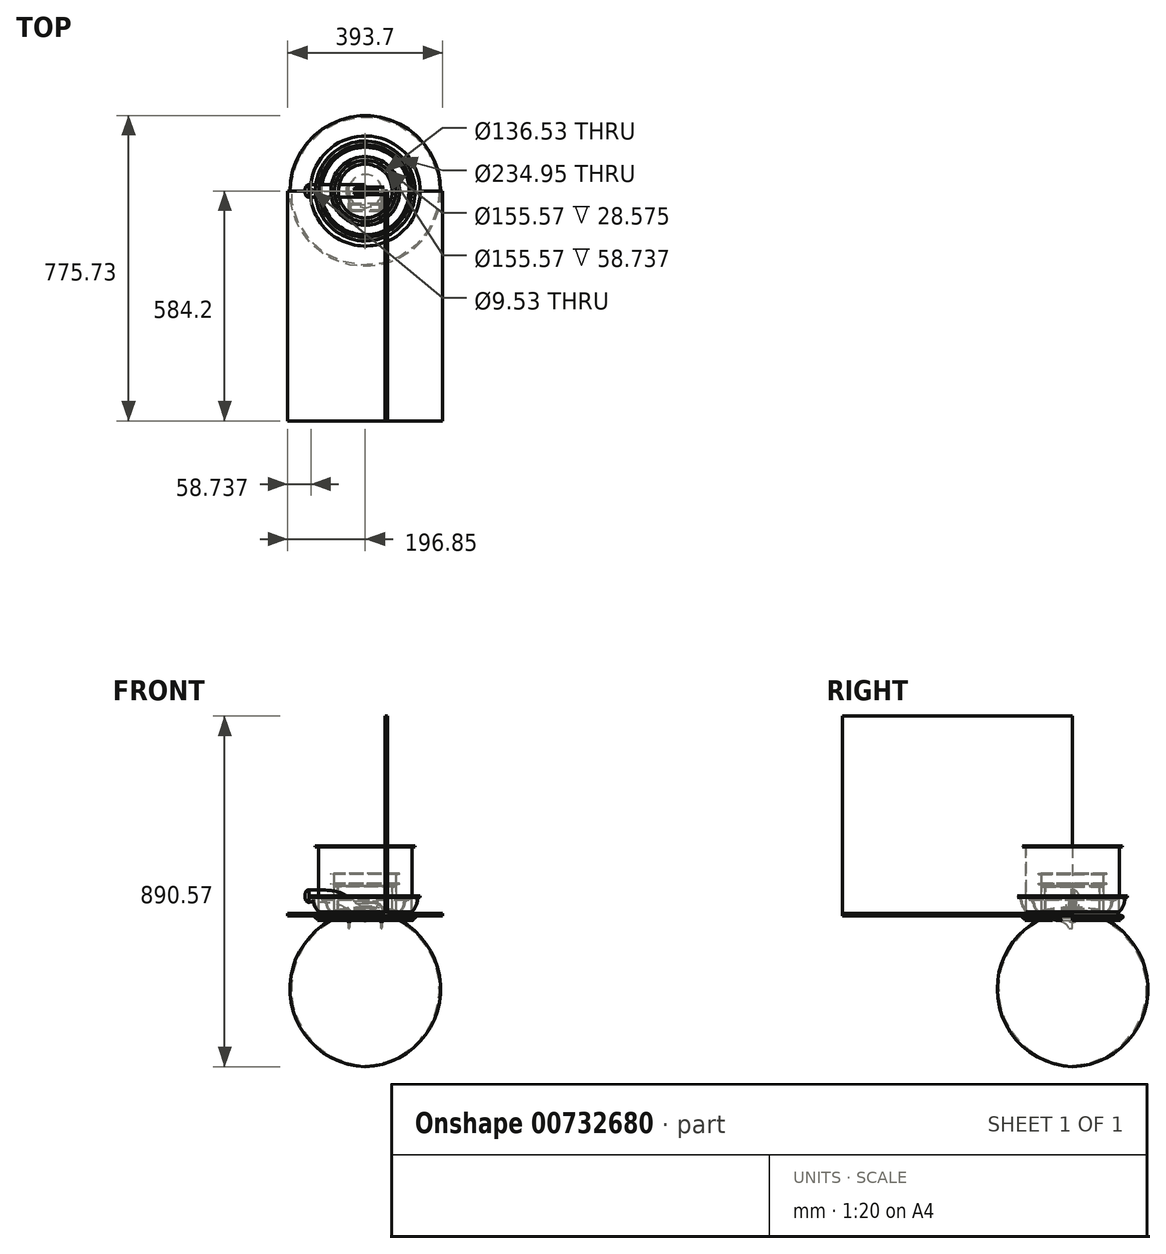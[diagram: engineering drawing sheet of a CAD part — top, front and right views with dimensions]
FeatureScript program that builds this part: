
annotation { "Feature Type Name" : "Feature", "Feature Type Description" : "" }
export const myFeature = defineFeature(function(context is Context, id is Id, definition is map)
    precondition{}
    {
        {
            var Q0;
            Q0=qCreatedBy(makeId("Front.planeOp"),FACE);
            var sketch = newSketch(context, id + "F0", { "sketchPlane" : qUnion([Q0])});
            skLineSegment(sketch, "E0", {"start": v(0, 0) * mm, "end": v(-61.91, 0) * mm});
            skLineSegment(sketch, "E1", {"start": v(-61.91, 0) * mm, "end": v(-69.85, 10.16) * mm});
            skLineSegment(sketch, "E2", {"start": v(-69.85, 10.16) * mm, "end": v(-69.85, 71.44) * mm});
            skLineSegment(sketch, "E3", {"start": v(-73.03, 74.61) * mm, "end": v(-77.79, 74.61) * mm});
            skLineSegment(sketch, "E4", {"start": v(-77.79, 74.61) * mm, "end": v(-77.79, 76.2) * mm});
            skLineSegment(sketch, "E5", {"start": v(-77.79, 76.2) * mm, "end": v(-71.44, 76.2) * mm});
            skLineSegment(sketch, "E6", {"start": v(-68.26, 73.02) * mm, "end": v(-68.26, 15.87) * mm});
            skLineSegment(sketch, "E7", {"start": v(-61.91, 9.52) * mm, "end": v(0, 9.53) * mm});
            skLineSegment(sketch, "E8", {"start": v(0, 9.53) * mm, "end": v(0, 0) * mm});
            skArc(sketch, "E9.filletArc", {"start": v(-68.26, 15.87) * mm, "mid": v(-66.4, 11.38) * mm, "end": v(-61.91, 9.52) * mm});
            skPoint(sketch, "E10.visualSharp", {"position": v(-69.85, 74.61) * mm});
            skArc(sketch, "E10.filletArc", {"start": v(-69.85, 71.44) * mm, "mid": v(-70.78, 73.68) * mm, "end": v(-73.03, 74.61) * mm});
            skPoint(sketch, "E11.visualSharp", {"position": v(-68.26, 76.2) * mm});
            skArc(sketch, "E11.filletArc", {"start": v(-68.26, 73.02) * mm, "mid": v(-69.2, 75.27) * mm, "end": v(-71.44, 76.2) * mm});
            skSolve(sketch);
        }
        {
            var Q0;
            Q0=makeQuery(id+"F0.imprint","IMPRINT",FACE,{"disambiguationData":[TD([[makeQuery(id+"F0.imprint","IMPRINT",EDGE,{"derivedFrom":sQuery(id+"F0.wireOp",EDGE,"E0")}),-1.0]])]});
            var Q1;
            Q1=sQuery(id+"F0.wireOp",EDGE,"E8");
            revolve(context, id + "F1", {"surfaceOperationType" : NewSurfaceOperationType.NEW, "entities" : qUnion([Q0]), "axis" : qUnion([Q1]), "revolveType" : RevolveType.FULL});
        }
        {
            var Q0;
            Q0=qCreatedBy(makeId("Front.planeOp"),FACE);
            var sketch = newSketch(context, id + "F2", { "sketchPlane" : qUnion([Q0])});
            skLineSegment(sketch, "E12", {"start": v(0, 0) * mm, "end": v(-71.44, 0) * mm});
            skLineSegment(sketch, "E13", {"start": v(-71.44, 0) * mm, "end": v(-79.38, 10.16) * mm});
            skLineSegment(sketch, "E14", {"start": v(-79.38, 10.16) * mm, "end": v(-79.38, 77.79) * mm});
            skLineSegment(sketch, "E15", {"start": v(-82.55, 80.96) * mm, "end": v(-87.31, 80.96) * mm});
            skLineSegment(sketch, "E16", {"start": v(-87.31, 80.96) * mm, "end": v(-87.31, 82.55) * mm});
            skLineSegment(sketch, "E17", {"start": v(-87.31, 82.55) * mm, "end": v(-80.96, 82.55) * mm});
            skLineSegment(sketch, "E18", {"start": v(-77.79, 79.38) * mm, "end": v(-77.79, 15.88) * mm});
            skLineSegment(sketch, "E19", {"start": v(-71.44, 9.52) * mm, "end": v(0, 9.53) * mm});
            skLineSegment(sketch, "E20", {"start": v(0, 9.53) * mm, "end": v(0, 0) * mm});
            skArc(sketch, "E21.filletArc", {"start": v(-77.79, 15.88) * mm, "mid": v(-75.93, 11.38) * mm, "end": v(-71.44, 9.53) * mm});
            skPoint(sketch, "E22.visualSharp", {"position": v(-79.38, 80.96) * mm});
            skArc(sketch, "E22.filletArc", {"start": v(-79.38, 77.79) * mm, "mid": v(-80.3, 80.03) * mm, "end": v(-82.55, 80.96) * mm});
            skPoint(sketch, "E23.visualSharp", {"position": v(-77.79, 82.55) * mm});
            skArc(sketch, "E23.filletArc", {"start": v(-77.79, 79.38) * mm, "mid": v(-78.72, 81.62) * mm, "end": v(-80.96, 82.55) * mm});
            skSolve(sketch);
        }
        {
            var Q0;
            Q0 = qSketchRegion(id + "F2", true);
            var Q1;
            Q1=sQuery(id+"F2.wireOp",EDGE,"E20");
            revolve(context, id + "F3", {"surfaceOperationType" : NewSurfaceOperationType.NEW, "entities" : qUnion([Q0]), "axis" : qUnion([Q1]), "revolveType" : RevolveType.FULL});
        }
        {
            var Q0;
            Q0=qCreatedBy(makeId("Front.planeOp"),FACE);
            var sketch = newSketch(context, id + "F4", { "sketchPlane" : qUnion([Q0])});
            skLineSegment(sketch, "E24", {"start": v(0, 0) * mm, "end": v(-71.44, 0) * mm});
            skLineSegment(sketch, "E25", {"start": v(-71.44, 0) * mm, "end": v(-79.38, 10.16) * mm});
            skLineSegment(sketch, "E26", {"start": v(-79.38, 10.16) * mm, "end": v(-79.38, 103.19) * mm});
            skLineSegment(sketch, "E27", {"start": v(-82.55, 106.36) * mm, "end": v(-87.31, 106.36) * mm});
            skLineSegment(sketch, "E28", {"start": v(-87.31, 106.36) * mm, "end": v(-87.31, 107.95) * mm});
            skLineSegment(sketch, "E29", {"start": v(-87.31, 107.95) * mm, "end": v(-80.96, 107.95) * mm});
            skLineSegment(sketch, "E30", {"start": v(-77.79, 104.78) * mm, "end": v(-77.79, 15.87) * mm});
            skLineSegment(sketch, "E31", {"start": v(-71.44, 9.52) * mm, "end": v(0, 9.53) * mm});
            skLineSegment(sketch, "E32", {"start": v(0, 9.53) * mm, "end": v(0, 0) * mm});
            skArc(sketch, "E33.filletArc", {"start": v(-77.79, 15.87) * mm, "mid": v(-75.93, 11.38) * mm, "end": v(-71.44, 9.52) * mm});
            skPoint(sketch, "E34.visualSharp", {"position": v(-79.38, 106.36) * mm});
            skArc(sketch, "E34.filletArc", {"start": v(-79.38, 103.19) * mm, "mid": v(-80.3, 105.43) * mm, "end": v(-82.55, 106.36) * mm});
            skPoint(sketch, "E35.visualSharp", {"position": v(-77.79, 107.95) * mm});
            skArc(sketch, "E35.filletArc", {"start": v(-77.79, 104.78) * mm, "mid": v(-78.72, 107.02) * mm, "end": v(-80.96, 107.95) * mm});
            skSolve(sketch);
        }
        {
            var Q0;
            Q0 = qSketchRegion(id + "F4", true);
            var Q1;
            Q1=sQuery(id+"F4.wireOp",EDGE,"E32");
            revolve(context, id + "F5", {"surfaceOperationType" : NewSurfaceOperationType.NEW, "entities" : qUnion([Q0]), "axis" : qUnion([Q1]), "revolveType" : RevolveType.FULL});
        }
        {
            var Q0;
            Q0=qCreatedBy(makeId("Front.planeOp"),FACE);
            var sketch = newSketch(context, id + "F6", { "sketchPlane" : qUnion([Q0])});
            skFitSpline(sketch, "E36", {"points": [v(0, 0) * mm, v(-53.98, 39.09) * mm, v(-152.4, 50.8) * mm], "startDerivative": vector(-187.57, 165.8) * mm, "endDerivative": vector(-373.43, -7.39) * mm});
            skSolve(sketch);
        }
        {
            var Q0;
            Q0=qCreatedBy(makeId("Right.planeOp"),FACE);
            var sketch = newSketch(context, id + "F7", { "sketchPlane" : qUnion([Q0])});
            skCircle(sketch, "E37", {"center": v(0, 0) * mm, "radius": 15.88 * mm});
            skSolve(sketch);
        }
        {
            var Q0;
            Q0 = qSketchRegion(id + "F7", true);
            var Q1;
            Q1=sQuery(id+"F6.wireOp",EDGE,"E36");
            sweep(context, id + "F8", {"profiles" : qUnion([Q0]), "path" : qUnion([Q1]), "keepProfileOrientation" : true});
        }
        {
            var Q0;
            Q0=makeQuery(id+"F8.opSweep","CAP_EDGE",EDGE,{"disambiguationData":[OSD([sQuery(id+"F6.wireOp",VERTEX,"E36.end"),sQuery(id+"F7.wireOp",EDGE,"E37")])],"isStart":false});
            fillet(context, id + "F9", {"entities" : qUnion([Q0]), "radius" : 9.52 * mm, "tangentPropagation" : true, "allowEdgeOverflow" : false});
        }
        {
            var Q0;
            Q0=qCreatedBy(makeId("Top.planeOp"),FACE);
            var sketch = newSketch(context, id + "F10", { "sketchPlane" : qUnion([Q0])});
            skCircle(sketch, "E38", {"center": v(-138.11, 0) * mm, "radius": 4.76 * mm});
            skSolve(sketch);
        }
        {
            var Q0;
            Q0=makeQuery(id+"F10.imprint","IMPRINT",FACE,{"disambiguationData":[TD([[makeQuery(id+"F10.imprint","IMPRINT",EDGE,{"derivedFrom":sQuery(id+"F10.wireOp",EDGE,"E38")}),1.0]])]});
            extrude(context, id + "F11", {"entities" : qUnion([Q0]), "operationType" : NewBodyOperationType.REMOVE, "depth" : 76.2 * mm, "offsetDistance" : 25.4 * mm});
        }
        {
            var Q0;
            Q0=qCreatedBy(makeId("Front.planeOp"),FACE);
            var sketch = newSketch(context, id + "F12", { "sketchPlane" : qUnion([Q0])});
            skArc(sketch, "E39", {"start": v(0, 12.7) * mm, "mid": v(-38.34, 10.18) * mm, "end": v(-75.46, 0.28) * mm});
            skLineSegment(sketch, "E40", {"start": v(0, 0) * mm, "end": v(0, 12.7) * mm, "construction": true});
            skPoint(sketch, "E41.orphan", {"position": v(63.8, 0) * mm});
            skArc(sketch, "E42.0", {"start": v(0, 9.53) * mm, "mid": v(-35.13, 7.47) * mm, "end": v(-69.31, -0.9) * mm});
            skArc(sketch, "E43", {"start": v(-75.46, 0.28) * mm, "mid": v(-76.34, 0.78) * mm, "end": v(-77, 0) * mm});
            skLineSegment(sketch, "E44", {"start": v(-77, 0) * mm, "end": v(-77, -3.97) * mm});
            skLineSegment(sketch, "E45", {"start": v(-76.2, -4.76) * mm, "end": v(-71.44, -4.76) * mm});
            skLineSegment(sketch, "E46", {"start": v(-70.64, -5.56) * mm, "end": v(-70.64, -11.11) * mm});
            skLineSegment(sketch, "E47", {"start": v(-70.64, -11.11) * mm, "end": v(-69.85, -11.11) * mm});
            skLineSegment(sketch, "E48", {"start": v(-69.85, -11.11) * mm, "end": v(-69.85, -1.64) * mm});
            skPoint(sketch, "E49.start.orphan", {"position": v(-76.2, -1.08) * mm});
            skLineSegment(sketch, "E50", {"start": v(0, 12.7) * mm, "end": v(0, 9.53) * mm});
            skPoint(sketch, "E51.visualSharp", {"position": v(-77, -4.76) * mm});
            skArc(sketch, "E51.filletArc", {"start": v(-77, -3.97) * mm, "mid": v(-76.76, -4.53) * mm, "end": v(-76.2, -4.76) * mm});
            skPoint(sketch, "E52.visualSharp", {"position": v(-70.64, -4.76) * mm});
            skArc(sketch, "E52.filletArc", {"start": v(-70.64, -5.56) * mm, "mid": v(-70.88, -5) * mm, "end": v(-71.44, -4.76) * mm});
            skPoint(sketch, "E53.visualSharp", {"position": v(-69.85, -1.08) * mm});
            skArc(sketch, "E53.filletArc", {"start": v(-69.31, -0.9) * mm, "mid": v(-69.7, -1.18) * mm, "end": v(-69.85, -1.64) * mm});
            skSolve(sketch);
        }
        {
            var Q0;
            Q0=makeQuery(id+"F12.imprint","IMPRINT",FACE,{"disambiguationData":[TD([[makeQuery(id+"F12.imprint","IMPRINT",EDGE,{"derivedFrom":sQuery(id+"F12.wireOp",EDGE,"E39")}),1.0]])]});
            var Q1;
            Q1=sQuery(id+"F12.wireOp",EDGE,"E40");
            revolve(context, id + "F13", {"surfaceOperationType" : NewSurfaceOperationType.NEW, "entities" : qUnion([Q0]), "axis" : qUnion([Q1]), "revolveType" : RevolveType.FULL});
        }
        {
            var Q0;
            Q0=qCreatedBy(makeId("Front.planeOp"),FACE);
            var sketch = newSketch(context, id + "F14", { "sketchPlane" : qUnion([Q0])});
            skArc(sketch, "E54", {"start": v(0, 15.88) * mm, "mid": v(-43.2, 11.94) * mm, "end": v(-84.98, 0.28) * mm});
            skLineSegment(sketch, "E55", {"start": v(0, 0) * mm, "end": v(0, 15.88) * mm, "construction": true});
            skPoint(sketch, "E56.orphan", {"position": v(84.74, 0.37) * mm});
            skArc(sketch, "E57.0", {"start": v(0, 12.7) * mm, "mid": v(-40, 9.29) * mm, "end": v(-78.85, -0.85) * mm});
            skArc(sketch, "E58", {"start": v(-84.98, 0.28) * mm, "mid": v(-85.87, 0.78) * mm, "end": v(-86.52, 0) * mm});
            skLineSegment(sketch, "E59", {"start": v(-86.52, 0) * mm, "end": v(-86.52, -3.97) * mm});
            skLineSegment(sketch, "E60", {"start": v(-85.73, -4.76) * mm, "end": v(-80.96, -4.76) * mm});
            skLineSegment(sketch, "E61", {"start": v(-80.17, -5.56) * mm, "end": v(-80.17, -11.11) * mm});
            skLineSegment(sketch, "E62", {"start": v(-80.17, -11.11) * mm, "end": v(-79.38, -11.11) * mm});
            skLineSegment(sketch, "E63", {"start": v(-79.38, -11.11) * mm, "end": v(-79.38, -1.6) * mm});
            skPoint(sketch, "E64.start.orphan", {"position": v(-85.73, -1.08) * mm});
            skLineSegment(sketch, "E65", {"start": v(0, 15.88) * mm, "end": v(0, 12.7) * mm});
            skPoint(sketch, "E66.visualSharp", {"position": v(-86.52, -4.76) * mm});
            skArc(sketch, "E66.filletArc", {"start": v(-86.52, -3.97) * mm, "mid": v(-86.29, -4.53) * mm, "end": v(-85.73, -4.76) * mm});
            skPoint(sketch, "E67.visualSharp", {"position": v(-80.17, -4.76) * mm});
            skArc(sketch, "E67.filletArc", {"start": v(-80.17, -5.56) * mm, "mid": v(-80.4, -5) * mm, "end": v(-80.96, -4.76) * mm});
            skPoint(sketch, "E68.visualSharp", {"position": v(-79.38, -1.04) * mm});
            skArc(sketch, "E68.filletArc", {"start": v(-78.85, -0.85) * mm, "mid": v(-79.23, -1.14) * mm, "end": v(-79.38, -1.6) * mm});
            skLineSegment(sketch, "E69", {"start": v(0, 15.88) * mm, "end": v(-46.26, 15.87) * mm, "construction": true});
            skSolve(sketch);
        }
        {
            var Q0;
            Q0=makeQuery(id+"F14.imprint","IMPRINT",FACE,{"disambiguationData":[TD([[makeQuery(id+"F14.imprint","IMPRINT",EDGE,{"derivedFrom":sQuery(id+"F14.wireOp",EDGE,"E54")}),1.0]])]});
            var Q1;
            Q1=sQuery(id+"F14.wireOp",EDGE,"E55");
            revolve(context, id + "F15", {"surfaceOperationType" : NewSurfaceOperationType.NEW, "entities" : qUnion([Q0]), "axis" : qUnion([Q1]), "revolveType" : RevolveType.FULL});
        }
        {
            var Q0;
            Q0=qCreatedBy(makeId("Front.planeOp"),FACE);
            var sketch = newSketch(context, id + "F16", { "sketchPlane" : qUnion([Q0])});
            skLineSegment(sketch, "E70.bottom", {"start": v(-47.63, 0) * mm, "end": v(-44.45, 0) * mm});
            skLineSegment(sketch, "E70.top", {"start": v(-22.23, 34.92) * mm, "end": v(22.23, 34.92) * mm});
            skLineSegment(sketch, "E70.left", {"start": v(-47.63, 0) * mm, "end": v(-47.63, 9.52) * mm});
            skLineSegment(sketch, "E70.right", {"start": v(47.62, 0) * mm, "end": v(47.62, 9.53) * mm});
            skPoint(sketch, "E71.visualSharp", {"position": v(-47.63, 34.93) * mm});
            skArc(sketch, "E71.filletArc", {"start": v(-22.23, 34.93) * mm, "mid": v(-40.19, 27.49) * mm, "end": v(-47.63, 9.52) * mm});
            skPoint(sketch, "E72.visualSharp", {"position": v(47.63, 34.92) * mm});
            skArc(sketch, "E72.filletArc", {"start": v(47.62, 9.53) * mm, "mid": v(40.19, 27.49) * mm, "end": v(22.23, 34.93) * mm});
            skLineSegment(sketch, "E73.0", {"start": v(44.45, 0) * mm, "end": v(44.45, 9.52) * mm});
            skLineSegment(sketch, "E73.1", {"start": v(-44.45, 0) * mm, "end": v(-44.45, 9.52) * mm});
            skArc(sketch, "E73.2", {"start": v(-22.23, 31.75) * mm, "mid": v(-37.94, 25.24) * mm, "end": v(-44.45, 9.52) * mm});
            skLineSegment(sketch, "E73.3", {"start": v(-22.23, 31.75) * mm, "end": v(22.23, 31.75) * mm});
            skArc(sketch, "E73.4", {"start": v(44.45, 9.52) * mm, "mid": v(37.94, 25.24) * mm, "end": v(22.23, 31.75) * mm});
            skLineSegment(sketch, "E74.trimOffspring", {"start": v(44.45, 0) * mm, "end": v(47.63, 0) * mm});
            skLineSegment(sketch, "E75", {"start": v(0, 0) * mm, "end": v(0, 34.92) * mm, "construction": true});
            skSolve(sketch);
        }
        {
            var Q0;
            Q0=makeQuery(id+"F16.imprint","IMPRINT",FACE,{"disambiguationData":[TD([[makeQuery(id+"F16.imprint","IMPRINT",EDGE,{"derivedFrom":sQuery(id+"F16.wireOp",EDGE,"E70.bottom")}),1.0]])]});
            extrude(context, id + "F17", {"entities" : qUnion([Q0]), "depth" : 9.52 * mm, "offsetDistance" : 25.4 * mm, "hasSecondDirection" : true, "secondDirectionOppositeDirection" : true, "secondDirectionDepth" : 9.52 * mm});
        }
        {
            var Q0;
            Q0=makeQuery(id+"F17.opExtrude","SWEPT_FACE",FACE,{"disambiguationData":[OSD([sQuery(id+"F16.wireOp",EDGE,"E70.top")])]});
            var sketch = newSketch(context, id + "F18", { "sketchPlane" : qUnion([Q0])});
            skLineSegment(sketch, "E76.bottom", {"start": v(-26.99, 6.35) * mm, "end": v(26.99, 6.35) * mm});
            skLineSegment(sketch, "E76.top", {"start": v(-26.99, -6.35) * mm, "end": v(26.99, -6.35) * mm});
            skLineSegment(sketch, "E76.left", {"start": v(-31.75, 1.59) * mm, "end": v(-31.75, -1.59) * mm});
            skLineSegment(sketch, "E76.right", {"start": v(31.75, 1.59) * mm, "end": v(31.75, -1.59) * mm});
            skLineSegment(sketch, "E77", {"start": v(-31.75, 0) * mm, "end": v(31.75, 0) * mm, "construction": true});
            skLineSegment(sketch, "E78", {"start": v(0, 6.35) * mm, "end": v(0, -6.35) * mm, "construction": true});
            skPoint(sketch, "E79.visualSharp", {"position": v(-31.75, 6.35) * mm});
            skArc(sketch, "E79.filletArc", {"start": v(-26.99, 6.35) * mm, "mid": v(-30.36, 4.96) * mm, "end": v(-31.75, 1.59) * mm});
            skPoint(sketch, "E80.visualSharp", {"position": v(-31.75, -6.35) * mm});
            skArc(sketch, "E80.filletArc", {"start": v(-31.75, -1.59) * mm, "mid": v(-30.36, -4.96) * mm, "end": v(-26.99, -6.35) * mm});
            skPoint(sketch, "E81.visualSharp", {"position": v(31.75, 6.35) * mm});
            skArc(sketch, "E81.filletArc", {"start": v(31.75, 1.59) * mm, "mid": v(30.36, 4.96) * mm, "end": v(26.99, 6.35) * mm});
            skPoint(sketch, "E82.visualSharp", {"position": v(31.75, -6.35) * mm});
            skArc(sketch, "E82.filletArc", {"start": v(26.99, -6.35) * mm, "mid": v(30.36, -4.96) * mm, "end": v(31.75, -1.59) * mm});
            skSolve(sketch);
        }
        {
            var Q0;
            Q0 = qSketchRegion(id + "F18", true);
            extrude(context, id + "F19", {"entities" : qUnion([Q0]), "operationType" : NewBodyOperationType.ADD, "depth" : 3.17 * mm, "offsetDistance" : 25.4 * mm, "hasSecondDirection" : true, "secondDirectionOppositeDirection" : true, "secondDirectionDepth" : 9.52 * mm});
        }
        {
            var Q0;
            Q0=qCreatedBy(makeId("Front.planeOp"),FACE);
            var sketch = newSketch(context, id + "F20", { "sketchPlane" : qUnion([Q0])});
            skLineSegment(sketch, "E83", {"start": v(0, 0) * mm, "end": v(-111.13, 0) * mm});
            skLineSegment(sketch, "E84", {"start": v(-111.12, 0) * mm, "end": v(-119.06, 10.16) * mm});
            skLineSegment(sketch, "E85", {"start": v(-119.06, 10.16) * mm, "end": v(-119.06, 173.04) * mm});
            skLineSegment(sketch, "E86", {"start": v(-122.24, 176.21) * mm, "end": v(-127, 176.21) * mm});
            skLineSegment(sketch, "E87", {"start": v(-127, 176.21) * mm, "end": v(-127, 177.8) * mm});
            skLineSegment(sketch, "E88", {"start": v(-127, 177.8) * mm, "end": v(-120.65, 177.8) * mm});
            skLineSegment(sketch, "E89", {"start": v(-117.48, 174.63) * mm, "end": v(-117.47, 15.88) * mm});
            skLineSegment(sketch, "E90", {"start": v(-111.12, 9.52) * mm, "end": v(0, 9.53) * mm});
            skLineSegment(sketch, "E91", {"start": v(0, 9.53) * mm, "end": v(0, 0) * mm});
            skArc(sketch, "E92.filletArc", {"start": v(-117.47, 15.88) * mm, "mid": v(-115.62, 11.38) * mm, "end": v(-111.12, 9.53) * mm});
            skPoint(sketch, "E93.visualSharp", {"position": v(-119.06, 176.21) * mm});
            skArc(sketch, "E93.filletArc", {"start": v(-119.06, 173.04) * mm, "mid": v(-120, 175.28) * mm, "end": v(-122.24, 176.21) * mm});
            skPoint(sketch, "E94.visualSharp", {"position": v(-117.48, 177.8) * mm});
            skArc(sketch, "E94.filletArc", {"start": v(-117.48, 174.63) * mm, "mid": v(-118.4, 176.87) * mm, "end": v(-120.65, 177.8) * mm});
            skSolve(sketch);
        }
        {
            var Q0;
            Q0 = qSketchRegion(id + "F20", true);
            var Q1;
            Q1=sQuery(id+"F20.wireOp",EDGE,"E91");
            revolve(context, id + "F21", {"surfaceOperationType" : NewSurfaceOperationType.NEW, "entities" : qUnion([Q0]), "axis" : qUnion([Q1]), "revolveType" : RevolveType.FULL});
        }
        {
            var Q0;
            Q0=qCreatedBy(makeId("Front.planeOp"),FACE);
            var sketch = newSketch(context, id + "F22", { "sketchPlane" : qUnion([Q0])});
            skArc(sketch, "E95", {"start": v(0, 22.22) * mm, "mid": v(-64.07, 16.7) * mm, "end": v(-126.25, 0.27) * mm});
            skLineSegment(sketch, "E96", {"start": v(0, 0) * mm, "end": v(0, 22.23) * mm, "construction": true});
            skPoint(sketch, "E97.orphan", {"position": v(152.02, -10.07) * mm});
            skArc(sketch, "E98.0", {"start": v(0, 19.05) * mm, "mid": v(-60.88, 14.02) * mm, "end": v(-120.11, -0.94) * mm});
            skArc(sketch, "E99", {"start": v(-126.25, 0.27) * mm, "mid": v(-127.14, 0.78) * mm, "end": v(-127.8, 0) * mm});
            skLineSegment(sketch, "E100", {"start": v(-127.8, 0) * mm, "end": v(-127.8, -3.97) * mm});
            skLineSegment(sketch, "E101", {"start": v(-127, -4.76) * mm, "end": v(-122.24, -4.76) * mm});
            skLineSegment(sketch, "E102", {"start": v(-121.44, -5.56) * mm, "end": v(-121.44, -11.11) * mm});
            skLineSegment(sketch, "E103", {"start": v(-121.44, -11.11) * mm, "end": v(-120.65, -11.11) * mm});
            skLineSegment(sketch, "E104", {"start": v(-120.65, -11.11) * mm, "end": v(-120.65, -1.7) * mm});
            skPoint(sketch, "E105.start.orphan", {"position": v(-127, 181.72) * mm});
            skLineSegment(sketch, "E106", {"start": v(0, 22.23) * mm, "end": v(0, 19.05) * mm});
            skPoint(sketch, "E107.visualSharp", {"position": v(-127.8, -4.76) * mm});
            skArc(sketch, "E107.filletArc", {"start": v(-127.8, -3.97) * mm, "mid": v(-127.56, -4.53) * mm, "end": v(-127, -4.76) * mm});
            skPoint(sketch, "E108.visualSharp", {"position": v(-121.44, -4.76) * mm});
            skArc(sketch, "E108.filletArc", {"start": v(-121.44, -5.56) * mm, "mid": v(-121.68, -5) * mm, "end": v(-122.24, -4.76) * mm});
            skPoint(sketch, "E109.visualSharp", {"position": v(-120.65, -1.13) * mm});
            skArc(sketch, "E109.filletArc", {"start": v(-120.11, -0.94) * mm, "mid": v(-120.5, -1.23) * mm, "end": v(-120.65, -1.7) * mm});
            skLineSegment(sketch, "E110", {"start": v(86.92, 22.23) * mm, "end": v(0, 22.23) * mm, "construction": true});
            skSolve(sketch);
        }
        {
            var Q0;
            Q0 = qSketchRegion(id + "F22", true);
            var Q1;
            Q1=sQuery(id+"F22.wireOp",EDGE,"E96");
            revolve(context, id + "F23", {"surfaceOperationType" : NewSurfaceOperationType.NEW, "entities" : qUnion([Q0]), "axis" : qUnion([Q1]), "revolveType" : RevolveType.FULL});
        }
        {
            var Q0;
            Q0=qCreatedBy(makeId("Front.planeOp"),FACE);
            var sketch = newSketch(context, id + "F24", { "sketchPlane" : qUnion([Q0])});
            skLineSegment(sketch, "E111.bottom", {"start": v(-43.06, -31.75) * mm, "end": v(-39.88, -31.75) * mm});
            skLineSegment(sketch, "E111.top", {"start": v(-36.7, 0) * mm, "end": v(36.32, 0) * mm});
            skLineSegment(sketch, "E111.left", {"start": v(-43.06, -31.75) * mm, "end": v(-43.06, -6.35) * mm});
            skLineSegment(sketch, "E111.right", {"start": v(42.67, -31.75) * mm, "end": v(42.67, -6.35) * mm});
            skPoint(sketch, "E112.visualSharp", {"position": v(-43.06, 0) * mm});
            skArc(sketch, "E112.filletArc", {"start": v(-36.7, 0) * mm, "mid": v(-41.2, -1.86) * mm, "end": v(-43.06, -6.35) * mm});
            skPoint(sketch, "E113.visualSharp", {"position": v(42.67, 0) * mm});
            skArc(sketch, "E113.filletArc", {"start": v(42.67, -6.35) * mm, "mid": v(40.8, -1.86) * mm, "end": v(36.32, 0) * mm});
            skLineSegment(sketch, "E114.0", {"start": v(39.5, -31.75) * mm, "end": v(39.5, -6.35) * mm});
            skLineSegment(sketch, "E114.1", {"start": v(-36.7, -3.18) * mm, "end": v(36.32, -3.18) * mm});
            skLineSegment(sketch, "E114.2", {"start": v(-39.88, -31.75) * mm, "end": v(-39.88, -6.35) * mm});
            skPoint(sketch, "E115.visualSharp", {"position": v(-39.88, -3.18) * mm});
            skArc(sketch, "E115.filletArc", {"start": v(-36.7, -3.18) * mm, "mid": v(-38.96, -4.1) * mm, "end": v(-39.88, -6.35) * mm});
            skPoint(sketch, "E116.visualSharp", {"position": v(39.5, -3.18) * mm});
            skArc(sketch, "E116.filletArc", {"start": v(39.5, -6.35) * mm, "mid": v(38.56, -4.1) * mm, "end": v(36.32, -3.18) * mm});
            skLineSegment(sketch, "E117.trimOffspring", {"start": v(39.5, -31.75) * mm, "end": v(42.67, -31.75) * mm});
            skSolve(sketch);
        }
        {
            var Q0;
            Q0=makeQuery(id+"F24.imprint","IMPRINT",FACE,{"disambiguationData":[TD([[makeQuery(id+"F24.imprint","IMPRINT",EDGE,{"derivedFrom":sQuery(id+"F24.wireOp",EDGE,"E111.bottom")}),1.0]])]});
            extrude(context, id + "F25", {"entities" : qUnion([Q0]), "depth" : 50.8 * mm, "offsetDistance" : 25.4 * mm});
        }
        {
            var Q0;
            Q0=makeQuery(id+"F25.opExtrude","SWEPT_FACE",FACE,{"disambiguationData":[OSD([sQuery(id+"F24.wireOp",EDGE,"E111.left")])]});
            var sketch = newSketch(context, id + "F26", { "sketchPlane" : qUnion([Q0])});
            skLineSegment(sketch, "E118.bottom", {"start": v(0, 0) * mm, "end": v(31.75, 0) * mm});
            skLineSegment(sketch, "E118.top", {"start": v(0, -12.7) * mm, "end": v(22.23, -12.7) * mm});
            skLineSegment(sketch, "E118.left", {"start": v(0, 0) * mm, "end": v(0, -12.7) * mm});
            skLineSegment(sketch, "E118.right", {"start": v(31.75, 0) * mm, "end": v(31.75, -3.18) * mm});
            skPoint(sketch, "E119.visualSharp", {"position": v(31.75, -12.7) * mm});
            skArc(sketch, "E119.filletArc", {"start": v(22.23, -12.7) * mm, "mid": v(28.96, -9.91) * mm, "end": v(31.75, -3.18) * mm});
            skLineSegment(sketch, "E120", {"start": v(9.51, -31.75) * mm, "end": v(10.72, -28.65) * mm});
            skLineSegment(sketch, "E121", {"start": v(21.95, -17.67) * mm, "end": v(50.8, -7.17) * mm});
            skLineSegment(sketch, "E122", {"start": v(50.8, -7.17) * mm, "end": v(50.8, -31.75) * mm});
            skLineSegment(sketch, "E123", {"start": v(50.8, -31.75) * mm, "end": v(9.51, -31.75) * mm});
            skPoint(sketch, "E124.visualSharp", {"position": v(13.85, -20.62) * mm});
            skArc(sketch, "E124.filletArc", {"start": v(21.95, -17.67) * mm, "mid": v(15.15, -21.95) * mm, "end": v(10.72, -28.65) * mm});
            skSolve(sketch);
        }
        {
            var Q0;
            Q0 = qSketchRegion(id + "F26", true);
            extrude(context, id + "F27", {"entities" : qUnion([Q0]), "operationType" : NewBodyOperationType.REMOVE, "endBound" : BoundingType.THROUGH_ALL, "oppositeDirection" : true, "depth" : 25.4 * mm, "offsetDistance" : 25.4 * mm});
        }
        {
            var Q0;
            Q0=makeQuery(id+"F25.opExtrude","SWEPT_FACE",FACE,{"disambiguationData":[OSD([sQuery(id+"F24.wireOp",EDGE,"E111.top")])]});
            var sketch = newSketch(context, id + "F28", { "sketchPlane" : qUnion([Q0])});
            skLineSegment(sketch, "E125.bottom", {"start": v(33.14, -34.93) * mm, "end": v(-33.53, -34.93) * mm});
            skLineSegment(sketch, "E125.top", {"start": v(33.14, -47.62) * mm, "end": v(-33.53, -47.62) * mm});
            skLineSegment(sketch, "E125.left", {"start": v(36.32, -38.1) * mm, "end": v(36.32, -44.45) * mm});
            skLineSegment(sketch, "E125.right", {"start": v(-36.7, -38.1) * mm, "end": v(-36.7, -44.45) * mm});
            skLineSegment(sketch, "E126", {"start": v(36.32, -41.28) * mm, "end": v(-36.7, -41.28) * mm, "construction": true});
            skPoint(sketch, "E127.visualSharp", {"position": v(36.32, -34.93) * mm});
            skArc(sketch, "E127.filletArc", {"start": v(36.32, -38.1) * mm, "mid": v(35.39, -35.85) * mm, "end": v(33.14, -34.93) * mm});
            skPoint(sketch, "E128.visualSharp", {"position": v(36.32, -47.62) * mm});
            skArc(sketch, "E128.filletArc", {"start": v(33.14, -47.62) * mm, "mid": v(35.39, -46.7) * mm, "end": v(36.32, -44.45) * mm});
            skPoint(sketch, "E129.visualSharp", {"position": v(-36.7, -47.62) * mm});
            skArc(sketch, "E129.filletArc", {"start": v(-36.7, -44.45) * mm, "mid": v(-35.78, -46.7) * mm, "end": v(-33.53, -47.62) * mm});
            skPoint(sketch, "E130.visualSharp", {"position": v(-36.7, -34.93) * mm});
            skArc(sketch, "E130.filletArc", {"start": v(-33.53, -34.93) * mm, "mid": v(-35.78, -35.85) * mm, "end": v(-36.7, -38.1) * mm});
            skSolve(sketch);
        }
        {
            var Q0;
            Q0 = qSketchRegion(id + "F28", true);
            extrude(context, id + "F29", {"entities" : qUnion([Q0]), "operationType" : NewBodyOperationType.ADD, "depth" : 3.17 * mm, "offsetDistance" : 25.4 * mm, "hasSecondDirection" : true, "secondDirectionOppositeDirection" : true, "secondDirectionDepth" : 9.52 * mm});
        }
        {
            var Q0;
            Q0=qCreatedBy(makeId("Front.planeOp"),FACE);
            var sketch = newSketch(context, id + "F30", { "sketchPlane" : qUnion([Q0])});
            skLineSegment(sketch, "E131", {"start": v(0, 0) * mm, "end": v(-88.9, 0) * mm});
            skArc(sketch, "E132", {"start": v(-132.62, 41) * mm, "mid": v(-118.87, 11.85) * mm, "end": v(-88.9, 0) * mm});
            skLineSegment(sketch, "E133", {"start": v(0, 0) * mm, "end": v(0, 44.12) * mm, "construction": true});
            skLineSegment(sketch, "E134", {"start": v(-139.7, 47.62) * mm, "end": v(0, 47.62) * mm, "construction": true});
            skArc(sketch, "E135", {"start": v(-132.62, 41) * mm, "mid": v(-134.85, 45.7) * mm, "end": v(-139.7, 47.62) * mm});
            skArc(sketch, "E136.0", {"start": v(-129.46, 41.2) * mm, "mid": v(-132.68, 48.02) * mm, "end": v(-139.7, 50.8) * mm});
            skArc(sketch, "E136.1", {"start": v(-129.46, 41.2) * mm, "mid": v(-116.7, 14.17) * mm, "end": v(-88.9, 3.18) * mm});
            skLineSegment(sketch, "E136.2", {"start": v(0, 3.18) * mm, "end": v(-88.9, 3.18) * mm});
            skLineSegment(sketch, "E137", {"start": v(-139.7, 50.87) * mm, "end": v(-139.7, 47.62) * mm});
            skLineSegment(sketch, "E138", {"start": v(0, 3.18) * mm, "end": v(0, 0) * mm});
            skSolve(sketch);
        }
        {
            var Q0;
            Q0 = qSketchRegion(id + "F30", true);
            var Q1;
            Q1=sQuery(id+"F30.wireOp",EDGE,"E133");
            revolve(context, id + "F31", {"surfaceOperationType" : NewSurfaceOperationType.NEW, "entities" : qUnion([Q0]), "axis" : qUnion([Q1]), "revolveType" : RevolveType.FULL});
        }
        {
            var Q0;
            Q0=qCreatedBy(makeId("Front.planeOp"),FACE);
            var sketch = newSketch(context, id + "F32", { "sketchPlane" : qUnion([Q0])});
            skLineSegment(sketch, "E139", {"start": v(0, 0) * mm, "end": v(-63.5, 0) * mm});
            skArc(sketch, "E140", {"start": v(-100.58, 32.14) * mm, "mid": v(-88.04, 9.15) * mm, "end": v(-63.5, 0) * mm});
            skLineSegment(sketch, "E141", {"start": v(0, 0) * mm, "end": v(0, 19.33) * mm, "construction": true});
            skLineSegment(sketch, "E142", {"start": v(-111.13, 41.27) * mm, "end": v(79.73, 41.28) * mm, "construction": true});
            skArc(sketch, "E143", {"start": v(-100.58, 32.14) * mm, "mid": v(-104.15, 38.67) * mm, "end": v(-111.13, 41.27) * mm});
            skArc(sketch, "E144.0", {"start": v(-97.44, 32.6) * mm, "mid": v(-102.07, 41.07) * mm, "end": v(-111.12, 44.45) * mm});
            skArc(sketch, "E144.1", {"start": v(-97.44, 32.6) * mm, "mid": v(-85.96, 11.55) * mm, "end": v(-63.5, 3.17) * mm});
            skLineSegment(sketch, "E144.2", {"start": v(0, 3.18) * mm, "end": v(-63.5, 3.18) * mm});
            skLineSegment(sketch, "E145", {"start": v(-111.12, 44.45) * mm, "end": v(-111.12, 41.27) * mm});
            skLineSegment(sketch, "E146", {"start": v(0, 3.18) * mm, "end": v(0, 0) * mm});
            skSolve(sketch);
        }
        {
            var Q0;
            Q0 = qSketchRegion(id + "F32", true);
            var Q1;
            Q1=sQuery(id+"F32.wireOp",EDGE,"E141");
            revolve(context, id + "F33", {"surfaceOperationType" : NewSurfaceOperationType.NEW, "entities" : qUnion([Q0]), "axis" : qUnion([Q1]), "revolveType" : RevolveType.FULL});
        }
        {
            var Q0;
            Q0=qCreatedBy(makeId("Front.planeOp"),FACE);
            var sketch = newSketch(context, id + "F34", { "sketchPlane" : qUnion([Q0])});
            skLineSegment(sketch, "E147.bottom", {"start": v(-196.85, 6.35) * mm, "end": v(50.8, 6.35) * mm});
            skLineSegment(sketch, "E147.top", {"start": v(-196.85, 0) * mm, "end": v(196.85, 0) * mm});
            skLineSegment(sketch, "E147.left", {"start": v(-196.85, 6.35) * mm, "end": v(-196.85, 0) * mm});
            skLineSegment(sketch, "E147.right", {"start": v(196.85, 6.35) * mm, "end": v(196.85, 0) * mm});
            skLineSegment(sketch, "E148.bottom", {"start": v(57.15, 508) * mm, "end": v(50.8, 508) * mm});
            skLineSegment(sketch, "E148.left", {"start": v(57.15, 508) * mm, "end": v(57.15, 6.35) * mm});
            skLineSegment(sketch, "E148.right", {"start": v(50.8, 508) * mm, "end": v(50.8, 6.35) * mm});
            skLineSegment(sketch, "E149.trimOffspring", {"start": v(57.15, 6.35) * mm, "end": v(196.85, 6.35) * mm});
            skSolve(sketch);
        }
        {
            var Q0;
            Q0 = qSketchRegion(id + "F34", true);
            extrude(context, id + "F35", {"entities" : qUnion([Q0]), "depth" : 584.2 * mm, "offsetDistance" : 25.4 * mm});
        }
    });
